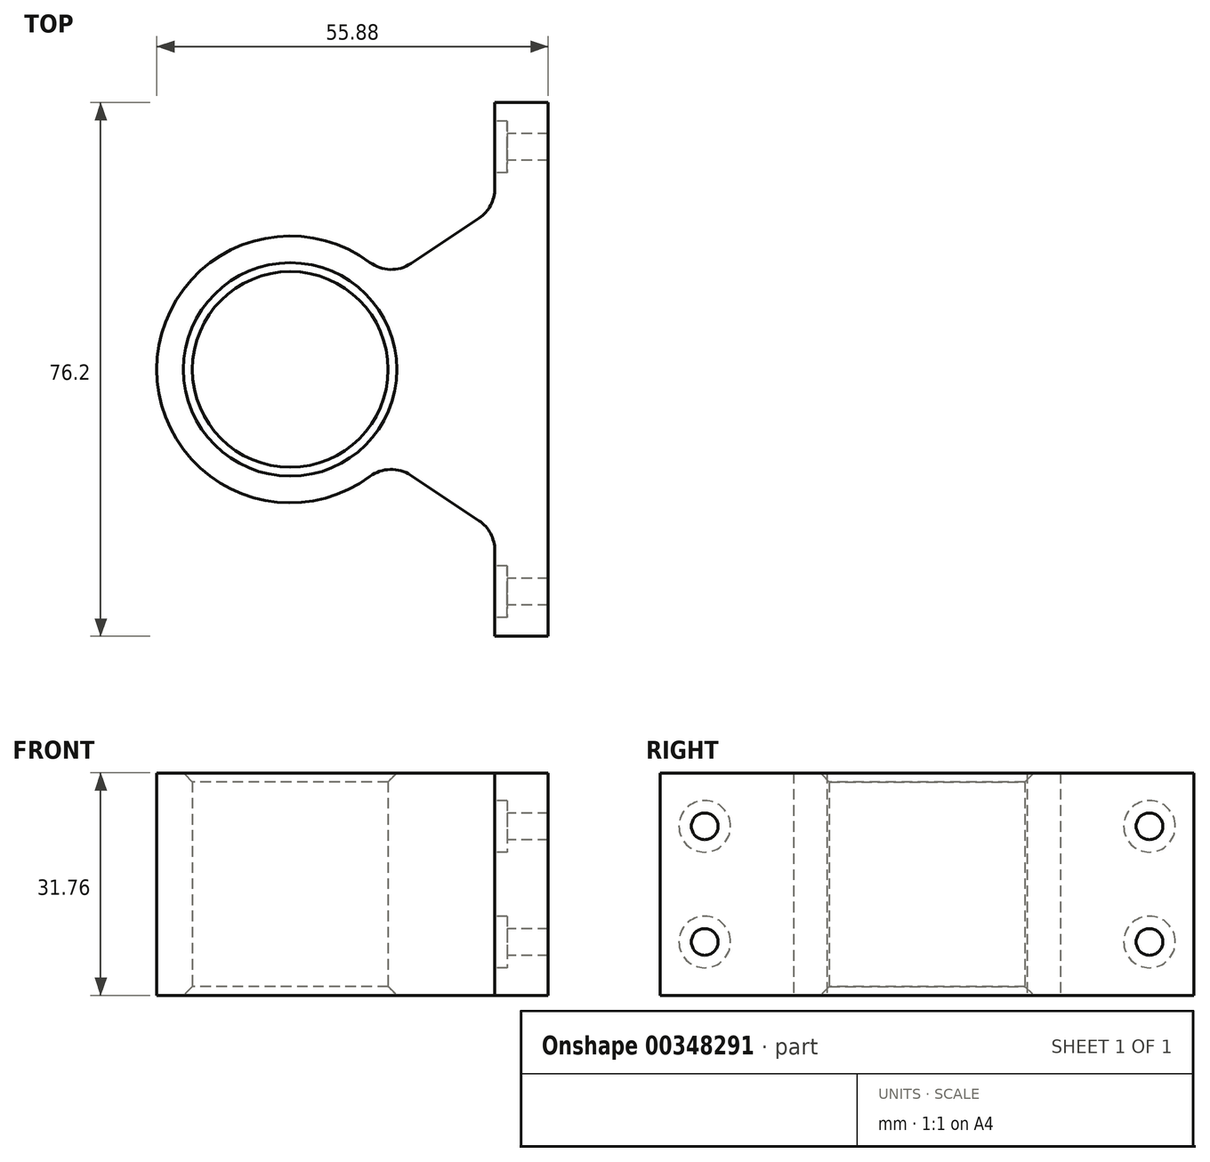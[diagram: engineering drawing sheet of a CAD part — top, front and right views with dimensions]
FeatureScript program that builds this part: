
annotation { "Feature Type Name" : "Feature", "Feature Type Description" : "" }
export const myFeature = defineFeature(function(context is Context, id is Id, definition is map)
    precondition{}
    {
        {
            var Q0;
            Q0=qCreatedBy(makeId("Top.planeOp"),FACE);
            var sketch = newSketch(context, id + "F0", { "sketchPlane" : qUnion([Q0])});
            skLineSegment(sketch, "E0.bottom", {"start": v(-3.8, 38.1) * mm, "end": v(3.81, 38.1) * mm});
            skLineSegment(sketch, "E0.top", {"start": v(-3.81, -38.1) * mm, "end": v(3.8, -38.1) * mm});
            skLineSegment(sketch, "E0.left", {"start": v(-3.8, 38.1) * mm, "end": v(-3.8, 23.11) * mm});
            skLineSegment(sketch, "E0.right", {"start": v(3.81, 38.1) * mm, "end": v(3.8, -38.1) * mm});
            skPoint(sketch, "E0.middle", {"position": v(0, 0) * mm});
            skCircle(sketch, "E1", {"center": v(-33.02, 0) * mm, "radius": 13.97 * mm});
            skArc(sketch, "E2", {"start": v(-19.05, 12.95) * mm, "mid": v(-52.07, 0) * mm, "end": v(-19.05, -12.95) * mm});
            skLineSegment(sketch, "E3", {"start": v(-3.81, 23.11) * mm, "end": v(-19.05, 12.95) * mm});
            skLineSegment(sketch, "E4.MirrorCS", {"start": v(-3.81, -23.11) * mm, "end": v(-19.05, -12.95) * mm});
            skLineSegment(sketch, "E5.trimOffspring", {"start": v(-3.81, -23.11) * mm, "end": v(-3.81, -38.1) * mm});
            skSolve(sketch);
        }
        {
            var Q0;
            Q0 = qSketchRegion(id + "F0", true);
            extrude(context, id + "F1", {"entities" : qUnion([Q0]), "endBound" : BoundingType.SYMMETRIC, "depth" : 31.75 * mm});
        }
        {
            var Q0;
            Q0=makeQuery(id+"F1.opExtrude","SWEPT_EDGE",EDGE,{"disambiguationData":[OSD([sQuery(id+"F0.wireOp",EDGE,"E2"),sQuery(id+"F0.wireOp",EDGE,"E4.MirrorCS")])]});
            var Q1;
            Q1=makeQuery(id+"F1.opExtrude","SWEPT_EDGE",EDGE,{"disambiguationData":[OSD([sQuery(id+"F0.wireOp",EDGE,"E4.MirrorCS"),sQuery(id+"F0.wireOp",EDGE,"E5.trimOffspring")])]});
            var Q2;
            Q2=makeQuery(id+"F1.opExtrude","SWEPT_EDGE",EDGE,{"disambiguationData":[OSD([sQuery(id+"F0.wireOp",EDGE,"E0.left"),sQuery(id+"F0.wireOp",EDGE,"E3")])]});
            var Q3;
            Q3=makeQuery(id+"F1.opExtrude","SWEPT_EDGE",EDGE,{"disambiguationData":[OSD([sQuery(id+"F0.wireOp",EDGE,"E2"),sQuery(id+"F0.wireOp",EDGE,"E3")])]});
            fillet(context, id + "F2", {"entities" : qUnion([Q0, Q1, Q2, Q3]), "radius" : 5.08 * mm, "tangentPropagation" : true, "allowEdgeOverflow" : false});
        }
        {
            var Q0;
            Q0=makeQuery(id+"F1.opExtrude","CAP_EDGE",EDGE,{"disambiguationData":[OSD([sQuery(id+"F0.wireOp",EDGE,"E1")])],"isStart":false});
            var Q1;
            Q1=makeQuery(id+"F1.opExtrude","CAP_EDGE",EDGE,{"disambiguationData":[OSD([sQuery(id+"F0.wireOp",EDGE,"E1")])],"isStart":true});
            chamfer(context, id + "F3", {"entities" : qUnion([Q0, Q1]), "chamferType" : ChamferType.OFFSET_ANGLE, "width" : 1.27 * mm, "oppositeDirection" : false, "angle" : 45 * degree, "tangentPropagation" : true});
        }
        {
            var Q0;
            Q0=makeQuery(id+"F1.opExtrude","SWEPT_FACE",FACE,{"disambiguationData":[OSD([sQuery(id+"F0.wireOp",EDGE,"E0.left")])]});
            var sketch = newSketch(context, id + "F4", { "sketchPlane" : qUnion([Q0])});
            skCircle(sketch, "E6", {"center": v(-31.75, 8.26) * mm, "radius": 3.68 * mm});
            skCircle(sketch, "E7.MirrorC", {"center": v(-31.75, -8.26) * mm, "radius": 3.68 * mm});
            skCircle(sketch, "E8.MirrorC", {"center": v(31.75, 8.26) * mm, "radius": 3.68 * mm});
            skCircle(sketch, "E9.MirrorC", {"center": v(31.75, -8.26) * mm, "radius": 3.68 * mm});
            skSolve(sketch);
        }
        {
            var Q0;
            Q0 = qSketchRegion(id + "F4", true);
            extrude(context, id + "F5", {"entities" : qUnion([Q0]), "operationType" : NewBodyOperationType.REMOVE, "oppositeDirection" : true, "depth" : 1.78 * mm});
        }
        {
            var Q0;
            Q0=makeQuery(id+"F1.opExtrude","SWEPT_FACE",FACE,{"disambiguationData":[OSD([sQuery(id+"F0.wireOp",EDGE,"E5.trimOffspring")])]});
            var sketch = newSketch(context, id + "F6", { "sketchPlane" : qUnion([Q0])});
            skCircle(sketch, "E10", {"center": v(31.75, 8.26) * mm, "radius": 1.9 * mm});
            skCircle(sketch, "E11.MirrorC", {"center": v(-31.75, 8.26) * mm, "radius": 1.9 * mm});
            skCircle(sketch, "E12.MirrorC", {"center": v(31.75, -8.26) * mm, "radius": 1.9 * mm});
            skCircle(sketch, "E13.MirrorC", {"center": v(-31.75, -8.26) * mm, "radius": 1.9 * mm});
            skSolve(sketch);
        }
        {
            var Q0;
            Q0 = qSketchRegion(id + "F6", true);
            extrude(context, id + "F7", {"entities" : qUnion([Q0]), "operationType" : NewBodyOperationType.REMOVE, "endBound" : BoundingType.THROUGH_ALL, "oppositeDirection" : true, "depth" : 25.4 * mm});
        }
    });
